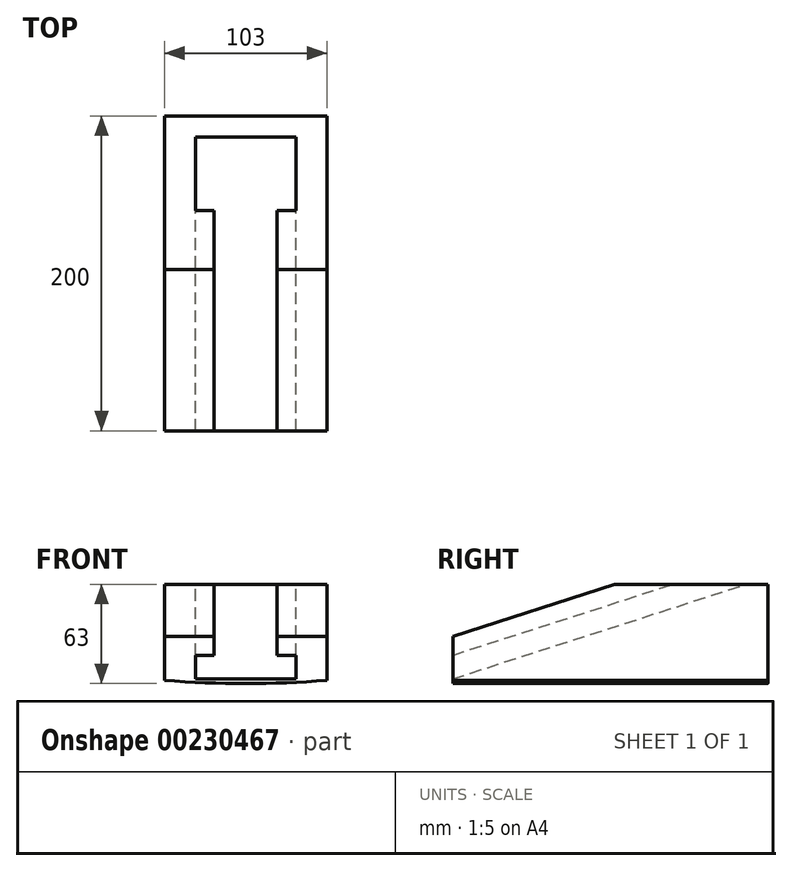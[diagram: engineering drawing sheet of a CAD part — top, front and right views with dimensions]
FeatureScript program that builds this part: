
annotation { "Feature Type Name" : "Feature", "Feature Type Description" : "" }
export const myFeature = defineFeature(function(context is Context, id is Id, definition is map)
    precondition{}
    {
        {
            var Q0;
            Q0=qCreatedBy(makeId("Right.planeOp"),FACE);
            var sketch = newSketch(context, id + "F0", { "sketchPlane" : qUnion([Q0])});
            skLineSegment(sketch, "E0", {"start": v(0, 0) * mm, "end": v(0, 3) * mm});
            skLineSegment(sketch, "E1", {"start": v(0, 3) * mm, "end": v(0, 18) * mm});
            skLineSegment(sketch, "E2", {"start": v(0, 18) * mm, "end": v(0, 30) * mm});
            skLineSegment(sketch, "E3", {"start": v(0, 30) * mm, "end": v(102.57, 63) * mm});
            skLineSegment(sketch, "E4", {"start": v(102.57, 63) * mm, "end": v(200, 63) * mm});
            skLineSegment(sketch, "E5", {"start": v(200, 63) * mm, "end": v(200, 0) * mm});
            skLineSegment(sketch, "E6", {"start": v(200, 0) * mm, "end": v(0, 0) * mm});
            skLineSegment(sketch, "E7", {"start": v(0, 18) * mm, "end": v(139.86, 63) * mm});
            skLineSegment(sketch, "E8", {"start": v(0, 3) * mm, "end": v(186.49, 63) * mm});
            skSolve(sketch);
        }
        {
            var Q0;
            Q0 = qSketchRegion(id + "F0", true);
            extrude(context, id + "F1", {"entities" : qUnion([Q0]), "endBound" : BoundingType.SYMMETRIC, "depth" : 103 * mm});
        }
        {
            var Q0;
            Q0=makeQuery(id+"F0.imprint","IMPRINT",FACE,{"disambiguationData":[TD([[makeQuery(id+"F0.imprint","IMPRINT",EDGE,{"derivedFrom":sQuery(id+"F0.wireOp",EDGE,"E2")}),-1.0]])]});
            extrude(context, id + "F2", {"entities" : qUnion([Q0]), "operationType" : NewBodyOperationType.REMOVE, "endBound" : BoundingType.SYMMETRIC, "oppositeDirection" : true, "depth" : 40 * mm});
        }
        {
            var Q0;
            Q0=makeQuery(id+"F0.imprint","IMPRINT",FACE,{"disambiguationData":[TD([[makeQuery(id+"F0.imprint","IMPRINT",EDGE,{"derivedFrom":sQuery(id+"F0.wireOp",EDGE,"E1")}),-1.0]])]});
            extrude(context, id + "F3", {"entities" : qUnion([Q0]), "operationType" : NewBodyOperationType.REMOVE, "endBound" : BoundingType.SYMMETRIC, "oppositeDirection" : true, "depth" : 64 * mm});
        }
        {
            var Q0;
            Q0=qCreatedBy(makeId("Front.planeOp"),FACE);
            var sketch = newSketch(context, id + "F4", { "sketchPlane" : qUnion([Q0])});
            skLineSegment(sketch, "E9", {"start": v(0, 0) * mm, "end": v(-51.5, 0) * mm});
            skLineSegment(sketch, "E10", {"start": v(0, 0) * mm, "end": v(51.5, 0) * mm});
            skLineSegment(sketch, "E11", {"start": v(51.5, 0) * mm, "end": v(51.5, 2) * mm});
            skLineSegment(sketch, "E12", {"start": v(-51.5, 0) * mm, "end": v(-51.5, 2) * mm});
            skArc(sketch, "E13", {"start": v(-51.5, 2) * mm, "mid": v(0, 0) * mm, "end": v(51.5, 2) * mm});
            skSolve(sketch);
        }
        {
            var Q0;
            {var subQ0=sQuery(id+"F4.wireOp",EDGE,"E9");Q0=makeQuery(id+"F4.imprint","IMPRINT",FACE,{"disambiguationData":[TD([[makeQuery(id+"F4.imprint","IMPRINT",EDGE,{"derivedFrom":subQ0}),-1.0]])]});}
            var Q1;
            {var subQ0=sQuery(id+"F4.wireOp",EDGE,"E10");Q1=makeQuery(id+"F4.imprint","IMPRINT",FACE,{"disambiguationData":[TD([[makeQuery(id+"F4.imprint","IMPRINT",EDGE,{"derivedFrom":subQ0}),1.0]])]});}
            extrude(context, id + "F5", {"entities" : qUnion([Q0, Q1]), "operationType" : NewBodyOperationType.REMOVE, "endBound" : BoundingType.THROUGH_ALL, "oppositeDirection" : true, "depth" : 25 * mm});
        }
    });
